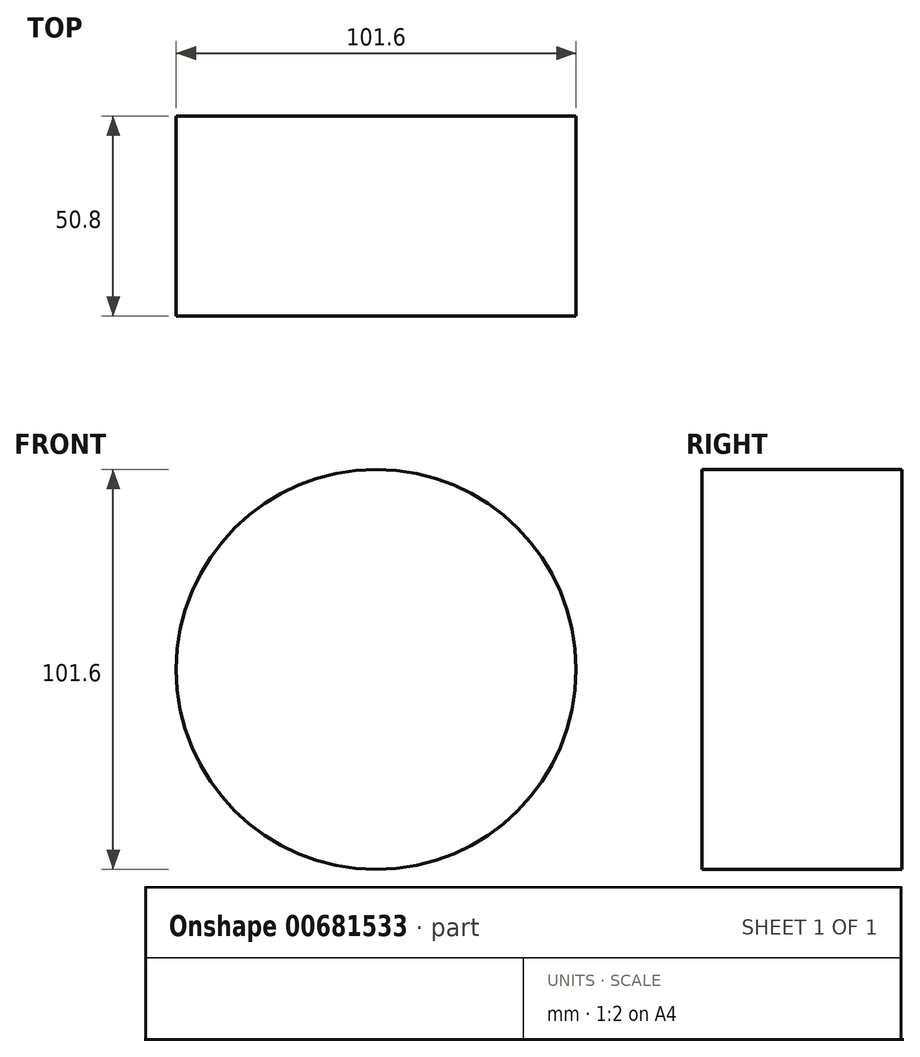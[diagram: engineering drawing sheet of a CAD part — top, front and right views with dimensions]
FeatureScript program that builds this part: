
annotation { "Feature Type Name" : "Feature", "Feature Type Description" : "" }
export const myFeature = defineFeature(function(context is Context, id is Id, definition is map)
    precondition{}
    {
        {
            var Q0;
            Q0=qCreatedBy(makeId("Front.planeOp"),FACE);
            var sketch = newSketch(context, id + "F0", { "sketchPlane" : qUnion([Q0])});
            skCircle(sketch, "E0", {"center": v(0, 0) * mm, "radius": 50.8 * mm});
            skCircle(sketch, "E1", {"center": v(0, 0) * mm, "radius": 38.1 * mm});
            skSolve(sketch);
        }
        {
            var Q0;
            Q0=makeQuery(id+"F0.imprint","IMPRINT",FACE,{"disambiguationData":[TD([[makeQuery(id+"F0.imprint","IMPRINT",EDGE,{"derivedFrom":sQuery(id+"F0.wireOp",EDGE,"E1")}),1.0]])]});
            var Q1;
            Q1=makeQuery(id+"F0.imprint","IMPRINT",FACE,{"disambiguationData":[TD([[makeQuery(id+"F0.imprint","IMPRINT",EDGE,{"derivedFrom":sQuery(id+"F0.wireOp",EDGE,"E0")}),1.0]])]});
            extrude(context, id + "F1", {"entities" : qUnion([Q0, Q1]), "depth" : 50.8 * mm, "offsetDistance" : 25.4 * mm});
        }
    });
